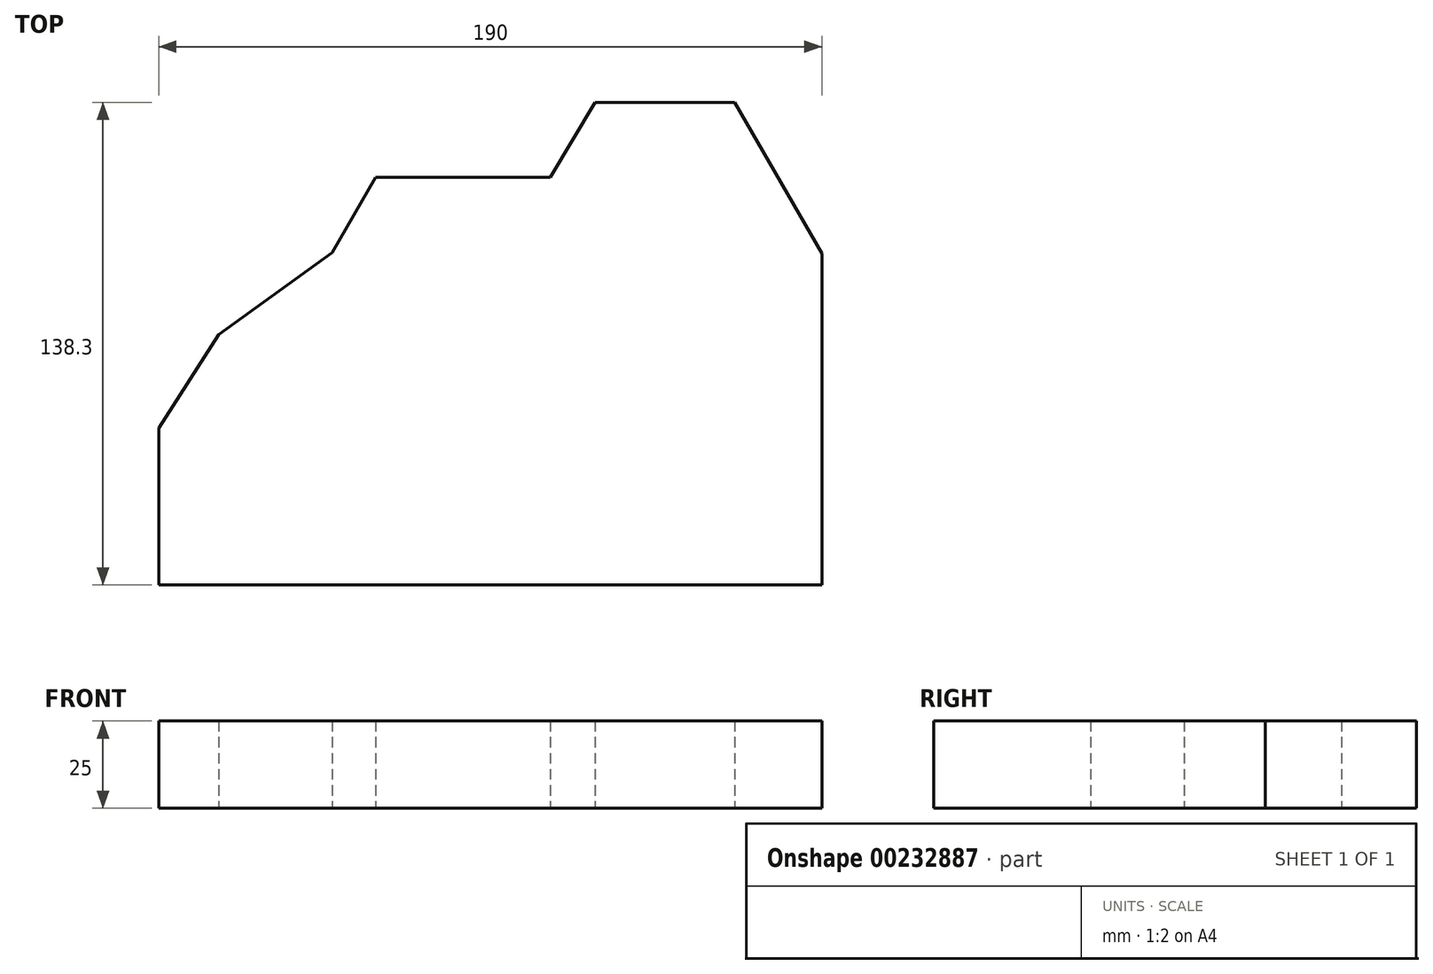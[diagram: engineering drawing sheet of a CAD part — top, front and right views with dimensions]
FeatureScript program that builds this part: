
annotation { "Feature Type Name" : "Feature", "Feature Type Description" : "" }
export const myFeature = defineFeature(function(context is Context, id is Id, definition is map)
    precondition{}
    {
        {
            var Q0;
            Q0=qCreatedBy(makeId("Top.planeOp"),FACE);
            var sketch = newSketch(context, id + "F0", { "sketchPlane" : qUnion([Q0])});
            skLineSegment(sketch, "E0", {"start": v(-98.78, -48.14) * mm, "end": v(91.22, -48.14) * mm});
            skLineSegment(sketch, "E1", {"start": v(-98.78, -48.14) * mm, "end": v(-98.78, -3.14) * mm});
            skLineSegment(sketch, "E2", {"start": v(91.22, -48.14) * mm, "end": v(91.22, 46.86) * mm});
            skLineSegment(sketch, "E3", {"start": v(91.22, 46.86) * mm, "end": v(66.22, 90.16) * mm});
            skLineSegment(sketch, "E4", {"start": v(91.22, 46.86) * mm, "end": v(91.22, 73.13) * mm});
            skLineSegment(sketch, "E5", {"start": v(66.22, 90.16) * mm, "end": v(26.22, 90.16) * mm});
            skLineSegment(sketch, "E6", {"start": v(26.22, 90.16) * mm, "end": v(13.35, 68.73) * mm});
            skLineSegment(sketch, "E7", {"start": v(13.35, 68.73) * mm, "end": v(-36.65, 68.73) * mm});
            skLineSegment(sketch, "E8", {"start": v(-36.65, 68.73) * mm, "end": v(-49.15, 47.08) * mm});
            skLineSegment(sketch, "E9", {"start": v(-49.15, 47.08) * mm, "end": v(-81.57, 23.64) * mm});
            skLineSegment(sketch, "E10", {"start": v(-81.57, 23.64) * mm, "end": v(-76.68, 27.18) * mm});
            skLineSegment(sketch, "E11", {"start": v(-98.78, -3.14) * mm, "end": v(-81.57, 23.64) * mm});
            skLineSegment(sketch, "E12", {"start": v(-49.15, 47.08) * mm, "end": v(-49.15, 90.33) * mm});
            skSolve(sketch);
        }
        {
            var Q0;
            Q0 = qSketchRegion(id + "F0", true);
            extrude(context, id + "F1", {"entities" : qUnion([Q0]), "depth" : 25 * mm});
        }
    });
